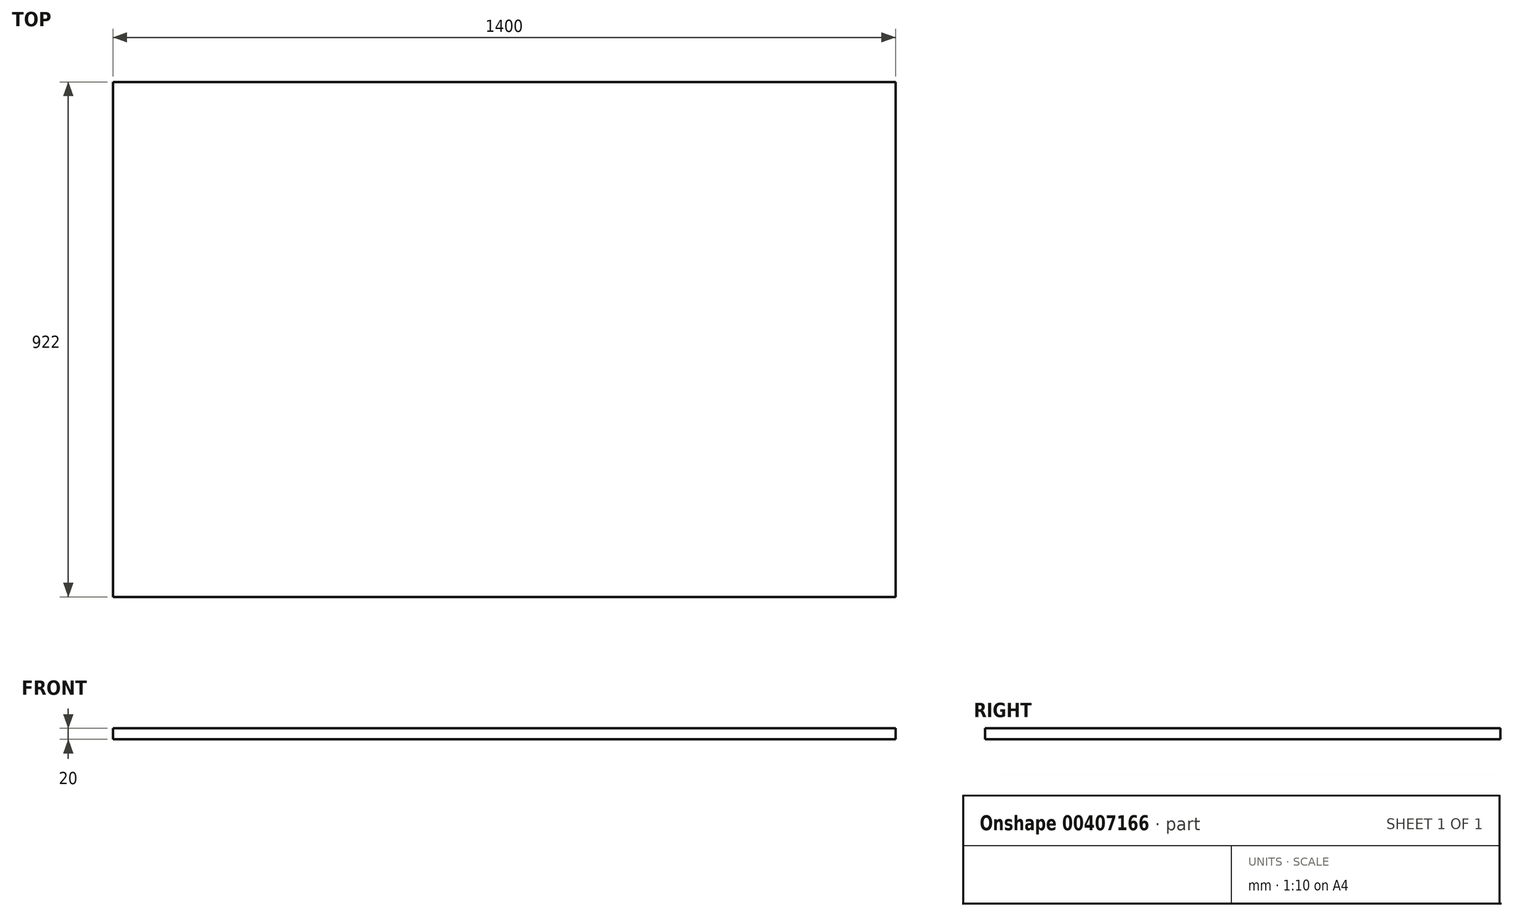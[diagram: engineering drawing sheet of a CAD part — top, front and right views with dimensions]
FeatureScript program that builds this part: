
annotation { "Feature Type Name" : "Feature", "Feature Type Description" : "" }
export const myFeature = defineFeature(function(context is Context, id is Id, definition is map)
    precondition{}
    {
        {
            var Q0;
            Q0=qCreatedBy(makeId("Top.planeOp"),FACE);
            var sketch = newSketch(context, id + "F0", { "sketchPlane" : qUnion([Q0])});
            skLineSegment(sketch, "E0.bottom", {"start": v(0, 0) * mm, "end": v(1400, 0) * mm});
            skLineSegment(sketch, "E0.top", {"start": v(0, 922) * mm, "end": v(1400, 922) * mm});
            skLineSegment(sketch, "E0.left", {"start": v(0, 0) * mm, "end": v(0, 922) * mm});
            skLineSegment(sketch, "E0.right", {"start": v(1400, 0) * mm, "end": v(1400, 922) * mm});
            skSolve(sketch);
        }
        {
            var Q0;
            Q0 = qSketchRegion(id + "F0", true);
            extrude(context, id + "F1", {"entities" : qUnion([Q0]), "depth" : 20 * mm});
        }
    });
